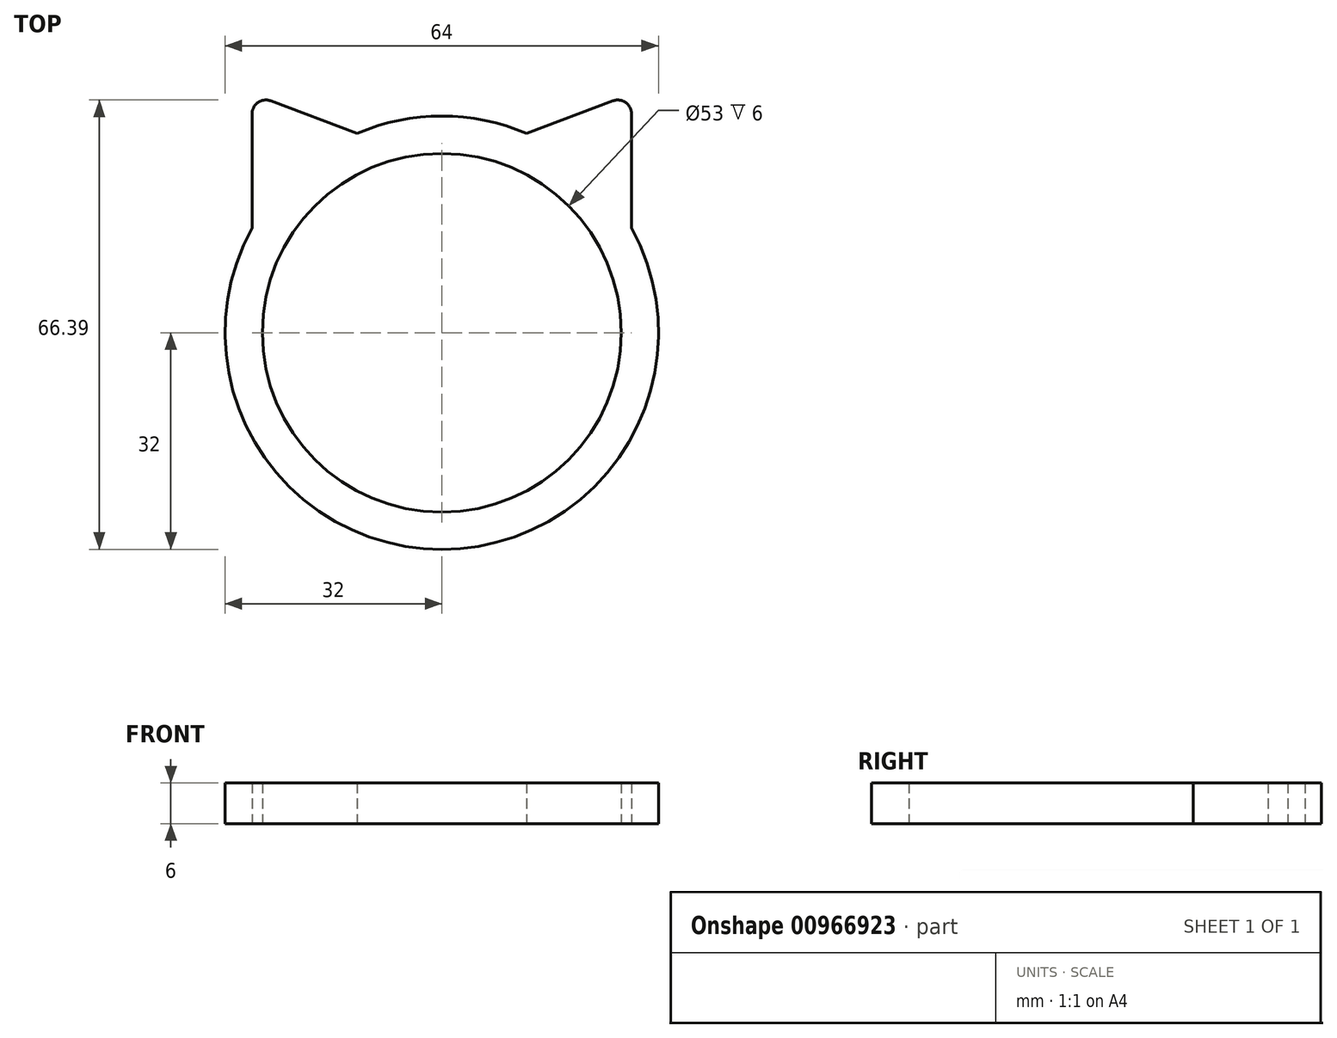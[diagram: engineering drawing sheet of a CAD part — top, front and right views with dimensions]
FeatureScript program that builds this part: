
annotation { "Feature Type Name" : "Feature", "Feature Type Description" : "" }
export const myFeature = defineFeature(function(context is Context, id is Id, definition is map)
    precondition{}
    {
        {
            var Q0;
            Q0=qCreatedBy(makeId("Top.planeOp"),FACE);
            var sketch = newSketch(context, id + "F0", { "sketchPlane" : qUnion([Q0])});
            skCircle(sketch, "E0", {"center": v(0, 0) * mm, "radius": 26.5 * mm});
            skCircle(sketch, "E1", {"center": v(0, 0) * mm, "radius": 32 * mm});
            skLineSegment(sketch, "E2", {"start": v(-28, 15.5) * mm, "end": v(-28, 35.27) * mm});
            skLineSegment(sketch, "E3", {"start": v(-28, 35.27) * mm, "end": v(-12.5, 29.46) * mm});
            skLineSegment(sketch, "E4.MirrorCS", {"start": v(28, 35.27) * mm, "end": v(12.5, 29.46) * mm});
            skLineSegment(sketch, "E5.MirrorCS", {"start": v(28, 15.5) * mm, "end": v(28, 35.27) * mm});
            skSolve(sketch);
        }
        {
            var Q0;
            {var subQ0=sQuery(id+"F0.wireOp",EDGE,"E2");Q0=makeQuery(id+"F0.imprint","IMPRINT",FACE,{"disambiguationData":[TD([[makeQuery(id+"F0.imprint","IMPRINT",EDGE,{"derivedFrom":subQ0}),-1.0]])]});}
            var Q1;
            Q1=makeQuery(id+"F0.imprint","IMPRINT",FACE,{"disambiguationData":[TD([[makeQuery(id+"F0.imprint","IMPRINT",EDGE,{"derivedFrom":sQuery(id+"F0.wireOp",EDGE,"E0")}),-1.0]])]});
            var Q2;
            {var subQ0=sQuery(id+"F0.wireOp",EDGE,"E4.MirrorCS");Q2=makeQuery(id+"F0.imprint","IMPRINT",FACE,{"disambiguationData":[TD([[makeQuery(id+"F0.imprint","IMPRINT",EDGE,{"derivedFrom":subQ0}),1.0]])]});}
            extrude(context, id + "F1", {"entities" : qUnion([Q0, Q1, Q2]), "depth" : 6 * mm, "offsetDistance" : 25 * mm});
        }
        {
            var Q0;
            Q0=makeQuery(id+"F1.opExtrude","SWEPT_EDGE",EDGE,{"disambiguationData":[OSD([sQuery(id+"F0.wireOp",EDGE,"E2"),sQuery(id+"F0.wireOp",EDGE,"E3")])]});
            var Q1;
            Q1=makeQuery(id+"F1.opExtrude","SWEPT_EDGE",EDGE,{"disambiguationData":[OSD([sQuery(id+"F0.wireOp",EDGE,"E4.MirrorCS"),sQuery(id+"F0.wireOp",EDGE,"E5.MirrorCS")])]});
            fillet(context, id + "F2", {"entities" : qUnion([Q0, Q1]), "radius" : 2 * mm, "tangentPropagation" : true, "allowEdgeOverflow" : false});
        }
    });
